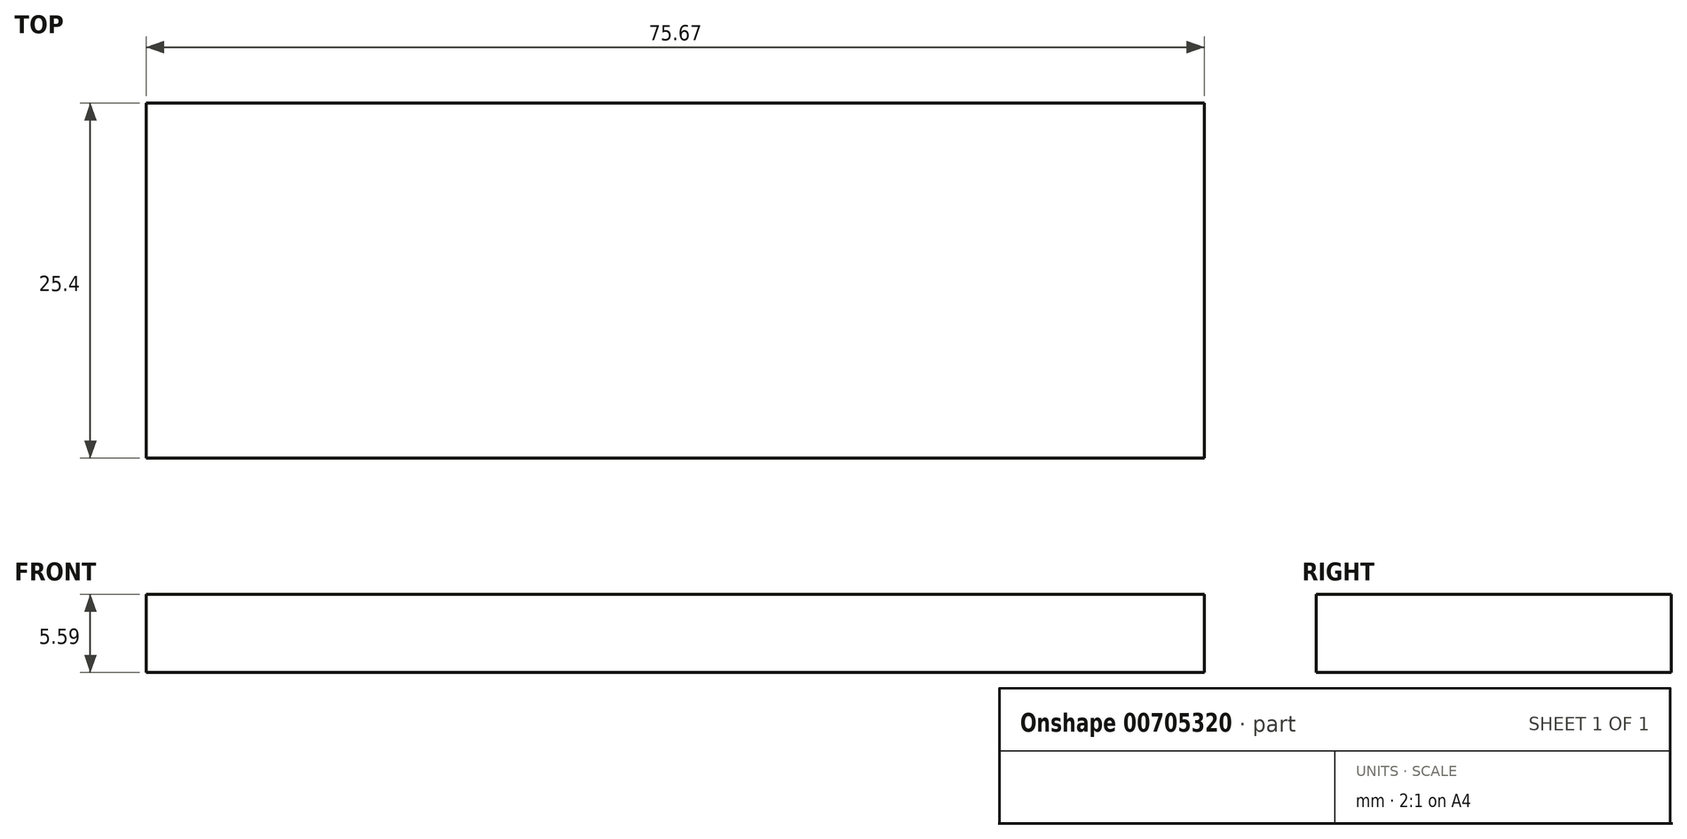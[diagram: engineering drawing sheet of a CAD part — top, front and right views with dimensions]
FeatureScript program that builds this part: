
annotation { "Feature Type Name" : "Feature", "Feature Type Description" : "" }
export const myFeature = defineFeature(function(context is Context, id is Id, definition is map)
    precondition{}
    {
        {
            var Q0;
            Q0=qCreatedBy(makeId("Front.planeOp"),FACE);
            var sketch = newSketch(context, id + "F0", { "sketchPlane" : qUnion([Q0])});
            skLineSegment(sketch, "E0.bottom", {"start": v(-75.67, 17.48) * mm, "end": v(0, 17.48) * mm});
            skLineSegment(sketch, "E0.top", {"start": v(-75.67, 11.89) * mm, "end": v(0, 11.89) * mm});
            skLineSegment(sketch, "E0.left", {"start": v(-75.67, 17.48) * mm, "end": v(-75.67, 11.89) * mm});
            skLineSegment(sketch, "E0.right", {"start": v(0, 17.48) * mm, "end": v(0, 11.89) * mm});
            skSolve(sketch);
        }
        {
            var Q0;
            Q0=makeQuery(id+"F0.imprint","IMPRINT",FACE,{"disambiguationData":[TD([[makeQuery(id+"F0.imprint","IMPRINT",EDGE,{"derivedFrom":sQuery(id+"F0.wireOp",EDGE,"E0.bottom")}),-1.0]])]});
            extrude(context, id + "F1", {"entities" : qUnion([Q0]), "depth" : 25.4 * mm, "offsetDistance" : 25.4 * mm});
        }
    });
